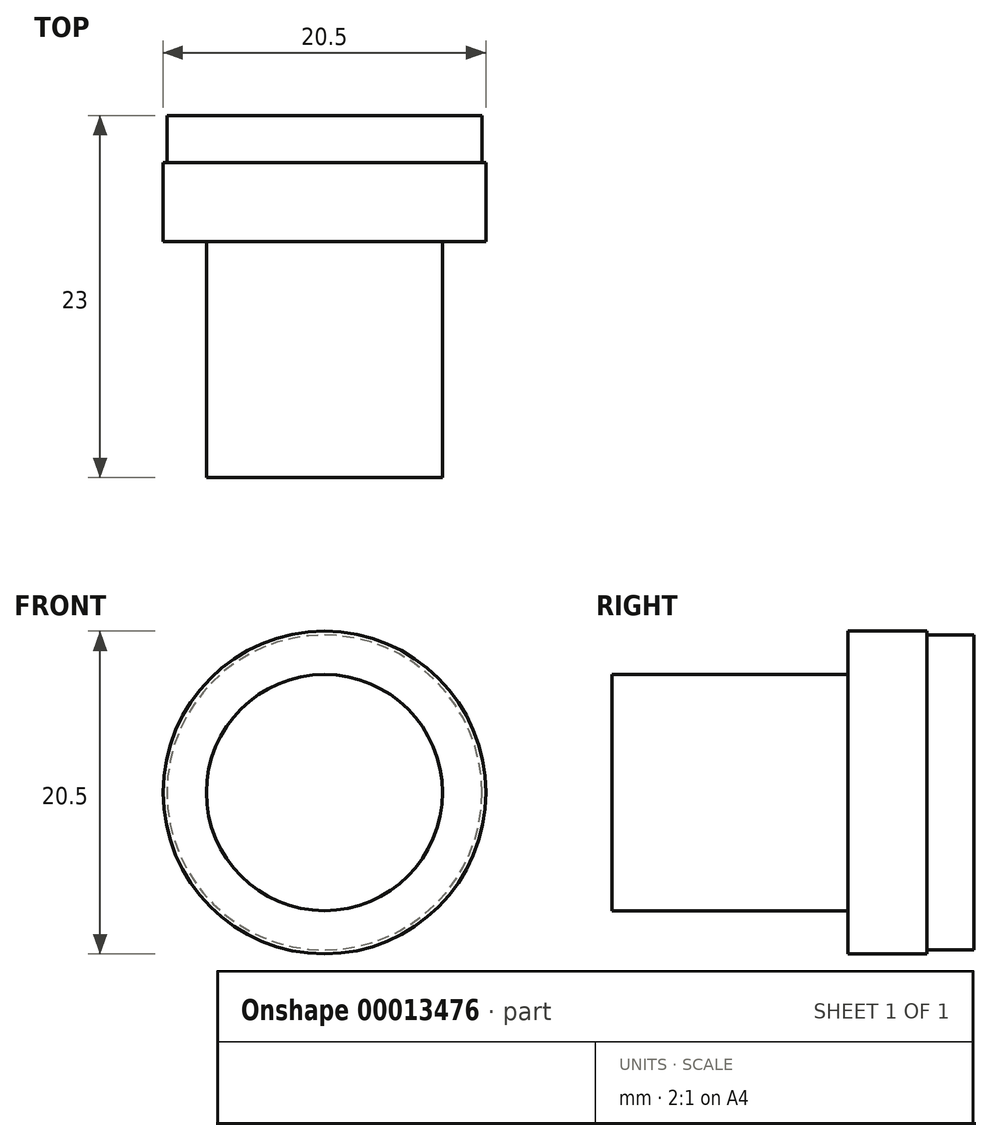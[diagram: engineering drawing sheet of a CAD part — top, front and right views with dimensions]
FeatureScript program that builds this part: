
annotation { "Feature Type Name" : "Feature", "Feature Type Description" : "" }
export const myFeature = defineFeature(function(context is Context, id is Id, definition is map)
    precondition{}
    {
        {
            var Q0;
            Q0=qCreatedBy(makeId("Front.planeOp"),FACE);
            var sketch = newSketch(context, id + "F0", { "sketchPlane" : qUnion([Q0])});
            skCircle(sketch, "E0", {"center": v(0, 0) * mm, "radius": 10 * mm});
            skSolve(sketch);
        }
        {
            var Q0;
            Q0 = qSketchRegion(id + "F0", true);
            extrude(context, id + "F1", {"entities" : qUnion([Q0]), "endBound" : BoundingType.SYMMETRIC, "depth" : 1 * mm});
        }
        {
            var Q0;
            Q0=makeQuery(id+"F1.opExtrude","CAP_FACE",FACE,{"disambiguationData":[OSD([sQuery(id+"F0.wireOp",EDGE,"E0")])],"isStart":false});
            var sketch = newSketch(context, id + "F2", { "sketchPlane" : qUnion([Q0])});
            skCircle(sketch, "E1", {"center": v(0, 0) * mm, "radius": 10.25 * mm});
            skSolve(sketch);
        }
        {
            var Q0;
            Q0=makeQuery(id+"F2.imprint","IMPRINT",FACE,{"disambiguationData":[TD([[makeQuery(id+"F2.imprint","IMPRINT",EDGE,{"derivedFrom":sQuery(id+"F2.wireOp",EDGE,"E1")}),1.0]])]});
            var Q1;
            Q1=makeQuery(id+"F2.imprint","IMPRINT",FACE,{"disambiguationData":[TD([[makeQuery(id+"F2.imprint","IMPRINT",EDGE,{"derivedFrom":makeQuery(id+"F1.opExtrude","CAP_EDGE",EDGE,{"disambiguationData":[OSD([sQuery(id+"F0.wireOp",EDGE,"E0")])],"isStart":false})}),1.0]])]});
            extrude(context, id + "F3", {"entities" : qUnion([Q0, Q1]), "operationType" : NewBodyOperationType.ADD, "depth" : 5 * mm});
        }
        {
            var Q0;
            Q0=makeQuery(id+"F3.opExtrude","CAP_FACE",FACE,{"disambiguationData":[OSD([sQuery(id+"F2.wireOp",EDGE,"E1")])],"isStart":false});
            var sketch = newSketch(context, id + "F4", { "sketchPlane" : qUnion([Q0])});
            skCircle(sketch, "E2", {"center": v(0, 0) * mm, "radius": 7.5 * mm});
            skSolve(sketch);
        }
        {
            var Q0;
            Q0 = qSketchRegion(id + "F4", true);
            extrude(context, id + "F5", {"entities" : qUnion([Q0]), "operationType" : NewBodyOperationType.ADD, "depth" : 15 * mm});
        }
        {
            var Q0;
            Q0=makeQuery(id+"F1.opExtrude","CAP_FACE",FACE,{"disambiguationData":[OSD([sQuery(id+"F0.wireOp",EDGE,"E0")])],"isStart":true});
            extrude(context, id + "F6", {"entities" : qUnion([Q0]), "operationType" : NewBodyOperationType.ADD, "depth" : 2 * mm});
        }
    });
